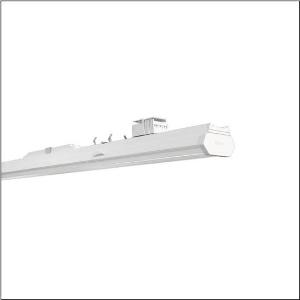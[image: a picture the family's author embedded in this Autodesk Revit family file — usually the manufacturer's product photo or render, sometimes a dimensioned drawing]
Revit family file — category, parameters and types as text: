
# Revit family: licross_r__11_protected_ho_51td12cn4exm_9b5e
name_source: partatom
category: Lighting Fixtures
units: mm (PartAtom-declared; Revit-internal decimal feet)

## family parameters
Cut with Voids When Loaded = No
Host = Face
Light Source = No
Part Type = Normal
Room Calculation Point = No
Round Connector Dimension = Use Diameter
Shared = No

## types (1)
- --- (1 x LED, 14240 lm, 77.6 W, 4000K)
    Apparent Load = 78 VA
    CIE Flux Codes = 70 91 97 98 100
    Color Rendering = 80
    Color Temperature = 4000K
    Default Elevation = 1800 mm
    Description = Licross® 11 Protected HO, luminaire insert, of sheet steel, galvanised, coil coated, white, length: 1.500mm, width: 90mm, height: 101mm, LED rated luminous flux: 14.240lm, light colour: 840, control gear: ON/OFF Multilumen, CLOi, with plug, 3-pole, with phase selection, mains connection: 220..240V, AC, 50/60Hz, start of lifetime: 78W, end of service life: 87W, halogen-free wiring, primary light control with lens, of plastic, primary optical cover: cover, of PMMA, light emission: direct distribution, primary light characteristic: symmetric, protection rating (complete): IP54, insulation class (complete): insulation class I (protective earthing), certification: CE, ENEC, VDE, UKCA, protection symbol: D if used in an environment with non-conductive dust loads with corresponding accessories, impact resistance: IK06, permissible ambient temperature for indoor applications: -35..+35°C, corresponds to IFS (International Featured Standards) requirements for safety and quality in the food industry, reducing of maximum allowable ambient temperature of 5°C with ceiling mounting, LABS conformity tested according to VDMA 24364:2018-05, packaging unit: 1 piece
    Height = 92 mm
    Lamp = 1 x LED
    Lamp Light Flux = 14240 lm
    Lamp Power = 77.6 W
    Lamp count = 1
    Length = 1500 mm
    Luminous efficacy = 184 lm/W
    Manufacturer = Siteco
    ModVariant = No
    Model = 51TD12CN4EXM
    Mounting Place = Ceiling
    Mounting Type = Pendant
    Number of Poles = 1
    OnlyDefault = Yes
    Power Factor = 1
    Product Name = Licross® 11 Protected HO
    Product group = luminaire insert
    ProductGroupID = 901
    Protection Class = Protection class I
    Protection Degree = IP 54
    RLX_Detail_Level = 1
    RLX_Emergency_Light_Flux = 0 lm
    RLX_Emergency_Type = 0
    RLX_Emergency_Type_DB = No
    RlxData = <blob elided: 22201 chars, md5=1aa21338>
    Socket = socket
    Standby Power = 0 W
    System Light Flux = 14240 lm
    System Power = 78 W
    Type Comments = factory setting: luminous flux: 100 % | (A | C | E) | 181 mA
    Type Image = l_1256145.jpg
    URL = http://relux.com
    VarID = @adj_055319
    Voltage = 0 V
    Weight = 0.00 kg
    Width = 88 mm

## geometry (parser evidence)
native form markers: Blend x4, Sweep x10
no freeform markers — native parametric forms only
